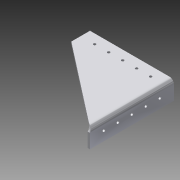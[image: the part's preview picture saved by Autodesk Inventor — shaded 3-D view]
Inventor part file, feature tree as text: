
AUTODESK INVENTOR PART (.ipt)
format: ipt  version: 2015 SP1 (Build 190203100, 203)  size: 160,256 bytes
history: native  units: in
note: dims shown in document units (in); Inventor stores cm internally (conversion verified against a paired STEP export)
features: other x7, hole x2, sheet_metal_op x2, sketch x1
ambient origin geometry x8: Origin, YZ Plane, XZ Plane, XY Plane, X Axis, Y Axis, Z Axis, Center Point
bodies: Solid1 (feature_tree)
feature tree (12):
  other  "<userpath>\Documents\2015 Offseason Chassis\West Coast Chassis Fall 2015\rivet(rv).xlsx"
  hole  "crossbar_rivet_holes"  [1 undecoded]
  other  "mounting_flange"
  hole  "bp_rivet_holes"  [1 undecoded]
  other  "face_sketch"
  other  "Plate1"
  other  "crossbar_rivet_holes_sketch"
  sketch  "Sketch3"  dims[d0=1.0in d1=4.5in d2=4.5in d3=0.12in d4=0.1406in d5=0.75in d6=0.375in d7=0.25in d8=0.5635in d9=0.12in d10=0.8108in d11=0.12in d12=0.06in d13=0.24in d14=0.12in d15=1.0in d16=90.0deg d17=0.12in d18=0.48in d19=0.12in d20=0.12in d21=0.5in d22=0.1406in d23=0.75in d24=0.375in d25=0.25in d26=0.5635in d27=0.12in d28=0.8108in]
  other  "Plate2"
  sheet_metal_op  "Bend1"
  sheet_metal_op  "Corner1"
  other  "bp_rivet_holes_sketch"
note: 2 required parameter values undecoded (feature->parameter linkage not recoverable at this tier; creation-order binding heuristic only, values carry confidence <= 0.55)
